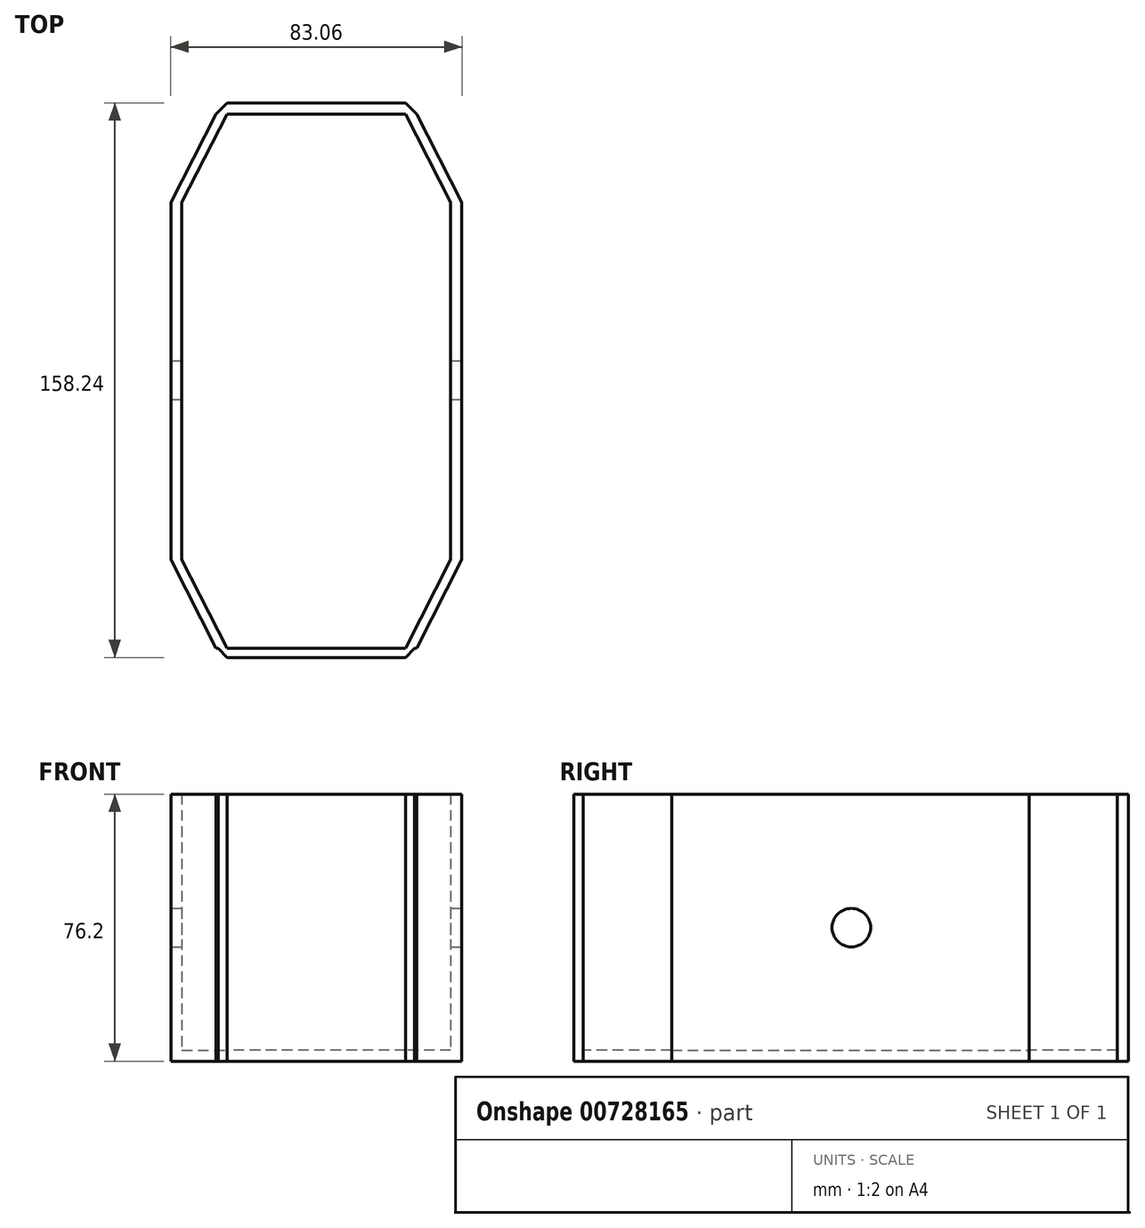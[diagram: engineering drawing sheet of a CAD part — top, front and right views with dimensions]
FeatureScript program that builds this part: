
annotation { "Feature Type Name" : "Feature", "Feature Type Description" : "" }
export const myFeature = defineFeature(function(context is Context, id is Id, definition is map)
    precondition{}
    {
        {
            var Q0;
            Q0=qCreatedBy(makeId("Top.planeOp"),FACE);
            var sketch = newSketch(context, id + "F0", { "sketchPlane" : qUnion([Q0])});
            skLineSegment(sketch, "E0", {"start": v(0, 75.95) * mm, "end": v(-25.42, 75.95) * mm});
            skLineSegment(sketch, "E1", {"start": v(-25.42, -76.55) * mm, "end": v(0, -76.55) * mm});
            skLineSegment(sketch, "E2.MirrorCS", {"start": v(0, 75.95) * mm, "end": v(25.42, 75.95) * mm});
            skLineSegment(sketch, "E3.MirrorCS", {"start": v(25.42, -76.55) * mm, "end": v(0, -76.55) * mm});
            skLineSegment(sketch, "E4", {"start": v(38.35, -51.28) * mm, "end": v(38.35, 50.68) * mm});
            skLineSegment(sketch, "E5.MirrorCS", {"start": v(-38.35, -51.28) * mm, "end": v(-38.35, 50.68) * mm});
            skLineSegment(sketch, "E6", {"start": v(-38.35, 50.68) * mm, "end": v(-25.42, 75.95) * mm});
            skLineSegment(sketch, "E7", {"start": v(25.42, 75.95) * mm, "end": v(38.35, 50.68) * mm});
            skLineSegment(sketch, "E8", {"start": v(38.35, -51.28) * mm, "end": v(25.42, -76.55) * mm});
            skLineSegment(sketch, "E9", {"start": v(-38.35, -51.28) * mm, "end": v(-25.42, -76.55) * mm});
            skPoint(sketch, "E10.MirrorCS.end.orphan", {"position": v(-38.35, 50.68) * mm});
            skPoint(sketch, "E11.orphan", {"position": v(-25.42, 50.68) * mm});
            skPoint(sketch, "E12.start.orphan", {"position": v(25.42, 50.68) * mm});
            skPoint(sketch, "E13.MirrorCS.end.orphan", {"position": v(-38.35, -51.28) * mm});
            skPoint(sketch, "E14.start.orphan", {"position": v(-25.42, -51.28) * mm});
            skLineSegment(sketch, "E15", {"start": v(25.42, 75.95) * mm, "end": v(28.6, 75.95) * mm});
            skLineSegment(sketch, "E16", {"start": v(38.35, 50.68) * mm, "end": v(41.53, 50.68) * mm});
            skLineSegment(sketch, "E17", {"start": v(41.53, 50.68) * mm, "end": v(28.6, 75.95) * mm});
            skLineSegment(sketch, "E18", {"start": v(38.35, -51.28) * mm, "end": v(41.53, -51.28) * mm});
            skLineSegment(sketch, "E19", {"start": v(41.53, -51.28) * mm, "end": v(41.53, 50.68) * mm});
            skLineSegment(sketch, "E20", {"start": v(25.42, -76.55) * mm, "end": v(28.6, -76.55) * mm});
            skLineSegment(sketch, "E21", {"start": v(28.6, -76.55) * mm, "end": v(41.53, -51.28) * mm});
            skLineSegment(sketch, "E22", {"start": v(-25.42, 75.95) * mm, "end": v(-28.6, 75.95) * mm});
            skLineSegment(sketch, "E23.MirrorCS", {"start": v(-41.53, 50.68) * mm, "end": v(-28.6, 75.95) * mm});
            skLineSegment(sketch, "E24.MirrorCS", {"start": v(-41.53, -51.28) * mm, "end": v(-41.53, 50.68) * mm});
            skLineSegment(sketch, "E25.MirrorCS", {"start": v(-28.6, -76.55) * mm, "end": v(-41.53, -51.28) * mm});
            skLineSegment(sketch, "E26.MirrorCS", {"start": v(-25.42, -76.55) * mm, "end": v(-28.6, -76.55) * mm});
            skPoint(sketch, "E27.MirrorCS.start.orphan", {"position": v(-25.42, 75.95) * mm});
            skLineSegment(sketch, "E28", {"start": v(-25.42, 75.95) * mm, "end": v(-25.42, 79.12) * mm});
            skLineSegment(sketch, "E29", {"start": v(25.42, 75.95) * mm, "end": v(25.42, 79.12) * mm});
            skLineSegment(sketch, "E30", {"start": v(25.42, 79.12) * mm, "end": v(-25.42, 79.12) * mm});
            skLineSegment(sketch, "E31", {"start": v(-28.6, 75.95) * mm, "end": v(-25.42, 79.12) * mm});
            skLineSegment(sketch, "E32", {"start": v(25.42, 79.12) * mm, "end": v(28.6, 75.95) * mm});
            skLineSegment(sketch, "E33.MirrorCS", {"start": v(25.42, -79.12) * mm, "end": v(-25.42, -79.12) * mm});
            skLineSegment(sketch, "E34.MirrorCS", {"start": v(-25.42, -75.95) * mm, "end": v(-25.42, -79.12) * mm});
            skLineSegment(sketch, "E35.MirrorCS", {"start": v(25.42, -75.95) * mm, "end": v(25.42, -79.12) * mm});
            skLineSegment(sketch, "E36.MirrorCS", {"start": v(25.42, -79.12) * mm, "end": v(28.6, -75.95) * mm});
            skLineSegment(sketch, "E37.MirrorCS", {"start": v(-28.6, -75.95) * mm, "end": v(-25.42, -79.12) * mm});
            skSolve(sketch);
        }
        {
            var Q0;
            Q0=makeQuery(id+"F0.imprint","IMPRINT",FACE,{"disambiguationData":[TD([[makeQuery(id+"F0.imprint","IMPRINT",EDGE,{"derivedFrom":sQuery(id+"F0.wireOp",EDGE,"E1")}),1.0]])]});
            extrude(context, id + "F1", {"entities" : qUnion([Q0]), "depth" : 3.17 * mm, "offsetDistance" : 25.4 * mm});
        }
        {
            var Q0;
            Q0 = qSketchRegion(id + "F0", true);
            extrude(context, id + "F2", {"entities" : qUnion([Q0]), "operationType" : NewBodyOperationType.ADD, "depth" : 76.2 * mm, "offsetDistance" : 25.4 * mm});
        }
        {
            var Q0;
            Q0=makeQuery(id+"F2.opExtrude","SWEPT_FACE",FACE,{"disambiguationData":[OSD([sQuery(id+"F0.wireOp",EDGE,"E19")])]});
            var sketch = newSketch(context, id + "F3", { "sketchPlane" : qUnion([Q0])});
            skLineSegment(sketch, "E38", {"start": v(0, 0) * mm, "end": v(0, 38.1) * mm});
            skCircle(sketch, "E39", {"center": v(0, 38.1) * mm, "radius": 5.5 * mm});
            skSolve(sketch);
        }
        {
            var Q0;
            Q0=makeQuery(id+"F3.imprint","IMPRINT",FACE,{"disambiguationData":[TD([[makeQuery(id+"F3.imprint","IMPRINT",EDGE,{"derivedFrom":sQuery(id+"F3.wireOp",EDGE,"E39")}),1.0]])]});
            extrude(context, id + "F4", {"entities" : qUnion([Q0]), "operationType" : NewBodyOperationType.REMOVE, "oppositeDirection" : true, "depth" : 106.68 * mm, "offsetDistance" : 25.4 * mm});
        }
    });
